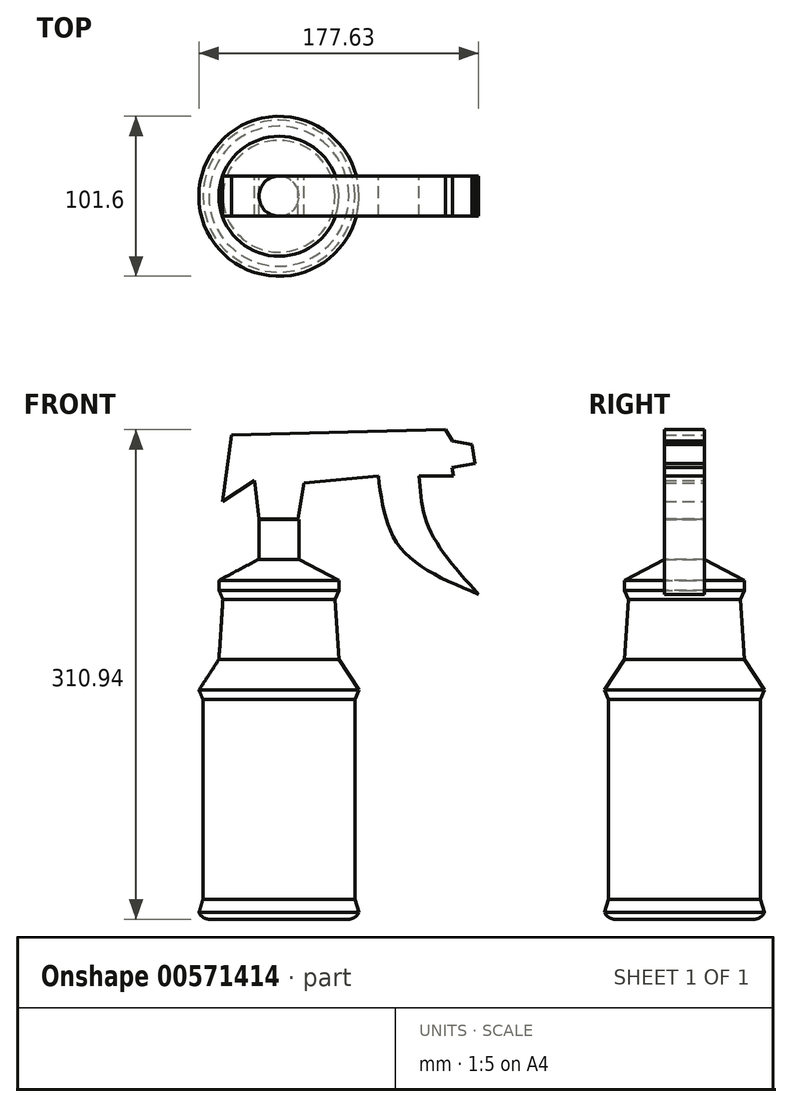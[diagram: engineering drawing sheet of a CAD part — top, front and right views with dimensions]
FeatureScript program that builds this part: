
annotation { "Feature Type Name" : "Feature", "Feature Type Description" : "" }
export const myFeature = defineFeature(function(context is Context, id is Id, definition is map)
    precondition{}
    {
        {
            var Q0;
            Q0=qCreatedBy(makeId("Top.planeOp"),FACE);
            var sketch = newSketch(context, id + "F0", { "sketchPlane" : qUnion([Q0])});
            skCircle(sketch, "E0", {"center": v(0, 0) * mm, "radius": 50.8 * mm});
            skSolve(sketch);
        }
        {
            var Q0;
            Q0=qCreatedBy(makeId("Front.planeOp"),FACE);
            var sketch = newSketch(context, id + "F1", { "sketchPlane" : qUnion([Q0])});
            skArc(sketch, "E1", {"start": v(44.45, 0) * mm, "mid": v(48.2, 1.27) * mm, "end": v(50.8, 4.25) * mm});
            skLineSegment(sketch, "E2", {"start": v(50.8, 4.25) * mm, "end": v(48.26, 12.7) * mm});
            skLineSegment(sketch, "E3", {"start": v(48.26, 12.7) * mm, "end": v(48.26, 139.7) * mm});
            skLineSegment(sketch, "E4", {"start": v(48.26, 139.7) * mm, "end": v(50.8, 145.52) * mm});
            skLineSegment(sketch, "E5", {"start": v(50.8, 145.52) * mm, "end": v(38.1, 165.1) * mm});
            skLineSegment(sketch, "E6", {"start": v(38.1, 165.1) * mm, "end": v(35.56, 203.12) * mm});
            skLineSegment(sketch, "E7", {"start": v(35.56, 203.12) * mm, "end": v(38.1, 208.94) * mm});
            skLineSegment(sketch, "E8", {"start": v(38.1, 208.94) * mm, "end": v(38.1, 215.29) * mm});
            skLineSegment(sketch, "E9", {"start": v(38.1, 215.29) * mm, "end": v(12.7, 228.66) * mm});
            skLineSegment(sketch, "E10", {"start": v(12.7, 228.66) * mm, "end": v(12.7, 254) * mm});
            skLineSegment(sketch, "E11", {"start": v(0, 0) * mm, "end": v(0, 396.58) * mm, "construction": true});
            skLineSegment(sketch, "E12", {"start": v(44.45, 0) * mm, "end": v(0, 0) * mm});
            skLineSegment(sketch, "E13", {"start": v(0, 0) * mm, "end": v(0, 254) * mm});
            skLineSegment(sketch, "E14", {"start": v(0, 254) * mm, "end": v(12.7, 254) * mm});
            skSolve(sketch);
        }
        {
            var Q0;
            Q0 = qSketchRegion(id + "F1", true);
            var Q1;
            Q1=sQuery(id+"F1.wireOp",EDGE,"E11");
            revolve(context, id + "F2", {"entities" : qUnion([Q0]), "axis" : qUnion([Q1]), "revolveType" : RevolveType.FULL});
        }
        {
            var Q0;
            Q0=qCreatedBy(makeId("Front.planeOp"),FACE);
            var sketch = newSketch(context, id + "F3", { "sketchPlane" : qUnion([Q0])});
            skLineSegment(sketch, "E15", {"start": v(-12.6, 254.18) * mm, "end": v(-15.42, 278.53) * mm});
            skLineSegment(sketch, "E16", {"start": v(-15.42, 278.53) * mm, "end": v(-35.74, 265.2) * mm});
            skLineSegment(sketch, "E17", {"start": v(-35.74, 265.2) * mm, "end": v(-30.23, 307.73) * mm});
            skLineSegment(sketch, "E18", {"start": v(-30.23, 307.73) * mm, "end": v(105.72, 310.94) * mm});
            skLineSegment(sketch, "E19", {"start": v(105.72, 310.94) * mm, "end": v(110.37, 303.84) * mm});
            skLineSegment(sketch, "E20", {"start": v(110.37, 303.84) * mm, "end": v(122.6, 301.62) * mm});
            skLineSegment(sketch, "E21", {"start": v(122.6, 301.62) * mm, "end": v(124.64, 289.4) * mm});
            skLineSegment(sketch, "E22", {"start": v(124.64, 289.4) * mm, "end": v(110.05, 286.96) * mm});
            skLineSegment(sketch, "E23", {"start": v(110.05, 286.96) * mm, "end": v(110.94, 281.63) * mm});
            skLineSegment(sketch, "E24", {"start": v(110.94, 281.63) * mm, "end": v(89.12, 281.63) * mm});
            skFitSpline(sketch, "E25", {"points": [v(89.12, 281.63) * mm, v(95.53, 248.06) * mm, v(126.83, 206.43) * mm], "startDerivative": vector(4.83, -74.94) * mm, "endDerivative": vector(68.36, -75.45) * mm});
            skFitSpline(sketch, "E26", {"points": [v(126.83, 206.43) * mm, v(76.98, 236.2) * mm, v(63.14, 281.63) * mm], "startDerivative": vector(-112.2, 46.47) * mm, "endDerivative": vector(-13.54, 104.92) * mm});
            skLineSegment(sketch, "E27", {"start": v(63.14, 281.63) * mm, "end": v(16.06, 277.05) * mm});
            skLineSegment(sketch, "E28", {"start": v(16.06, 277.05) * mm, "end": v(12.25, 254.54) * mm});
            skLineSegment(sketch, "E29", {"start": v(12.25, 254.54) * mm, "end": v(-12.6, 254.18) * mm});
            skSolve(sketch);
        }
        {
            var Q0;
            Q0 = qSketchRegion(id + "F3", true);
            extrude(context, id + "F4", {"entities" : qUnion([Q0]), "operationType" : NewBodyOperationType.ADD, "depth" : 12.7 * mm, "offsetDistance" : 25.4 * mm, "hasSecondDirection" : true, "secondDirectionOppositeDirection" : true, "secondDirectionDepth" : 12.7 * mm});
        }
    });
